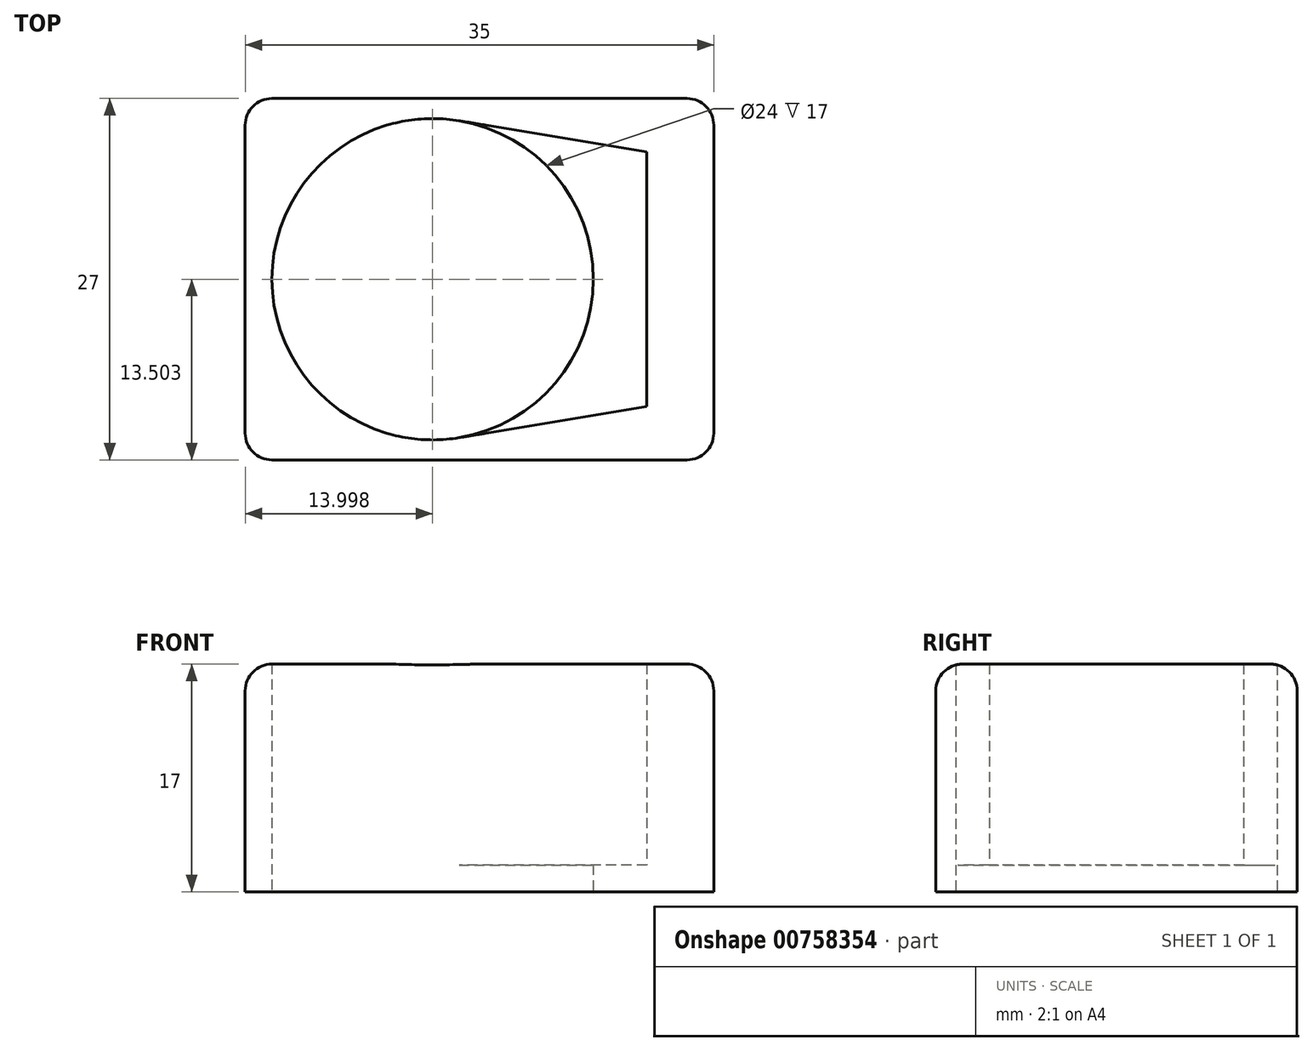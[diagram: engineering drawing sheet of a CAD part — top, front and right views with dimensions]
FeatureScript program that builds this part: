
annotation { "Feature Type Name" : "Feature", "Feature Type Description" : "" }
export const myFeature = defineFeature(function(context is Context, id is Id, definition is map)
    precondition{}
    {
        {
            var Q0;
            Q0=qCreatedBy(makeId("Top.planeOp"),FACE);
            var sketch = newSketch(context, id + "F0", { "sketchPlane" : qUnion([Q0])});
            skLineSegment(sketch, "E0", {"start": v(-0.7, 17.13) * mm, "end": v(-0.7, -1.87) * mm});
            skLineSegment(sketch, "E1", {"start": v(-0.7, 7.63) * mm, "end": v(-28.7, 7.63) * mm});
            skCircle(sketch, "E2", {"center": v(-16.7, 7.63) * mm, "radius": 12 * mm});
            skPoint(sketch, "E2.first.point", {"position": v(-8.44, 16.33) * mm});
            skPoint(sketch, "E2.third.point", {"position": v(-13.92, -4.04) * mm});
            skLineSegment(sketch, "E3", {"start": v(-0.7, 17.13) * mm, "end": v(-14.73, 19.47) * mm});
            skLineSegment(sketch, "E4", {"start": v(-0.7, -1.87) * mm, "end": v(-14.73, -4.2) * mm});
            skLineSegment(sketch, "E5.bottom", {"start": v(-30.7, 21.13) * mm, "end": v(4.3, 21.13) * mm});
            skLineSegment(sketch, "E5.top", {"start": v(-30.7, -5.87) * mm, "end": v(4.3, -5.87) * mm});
            skLineSegment(sketch, "E5.left", {"start": v(-30.7, 21.13) * mm, "end": v(-30.7, -5.87) * mm});
            skLineSegment(sketch, "E5.right", {"start": v(4.3, 21.13) * mm, "end": v(4.3, -5.87) * mm});
            skPoint(sketch, "E6", {"position": v(-28.7, 7.63) * mm});
            skPoint(sketch, "E7", {"position": v(-30.7, 7.63) * mm});
            skSolve(sketch);
        }
        {
            var Q0;
            {var subQ6=sQuery(id+"F0.wireOp",EDGE,"E3");Q0=makeQuery(id+"F0.imprint","IMPRINT",FACE,{"disambiguationData":[TD([[makeQuery(id+"F0.imprint","IMPRINT",EDGE,{"derivedFrom":subQ6}),-1.0]])]});}
            extrude(context, id + "F1", {"entities" : qUnion([Q0]), "depth" : 15 * mm, "offsetDistance" : 25 * mm});
        }
        {
            var Q0;
            {var subQ6=sQuery(id+"F0.wireOp",EDGE,"E3");Q0=makeQuery(id+"F0.imprint","IMPRINT",FACE,{"disambiguationData":[TD([[makeQuery(id+"F0.imprint","IMPRINT",EDGE,{"derivedFrom":subQ6}),-1.0]])]});}
            var Q1;
            {var subQ0=sQuery(id+"F0.wireOp",EDGE,"E2");var subQ1=sQuery(id+"F0.wireOp",EDGE,"E1");var subQ2=makeQuery(id+"F0.imprint","INTERSECT",VERTEX,{"disambiguationData":[OD(0.0)],"derivedFrom":[subQ1,subQ0]});Q1=makeQuery(id+"F0.imprint","IMPRINT",FACE,{"disambiguationData":[TD([[makeQuery(id+"F0.imprint","IMPRINT",EDGE,{"disambiguationData":[TD([[subQ2,1.0]])],"derivedFrom":subQ1}),1.0]])]});}
            var Q2;
            {var subQ0=sQuery(id+"F0.wireOp",EDGE,"E2");var subQ1=sQuery(id+"F0.wireOp",EDGE,"E1");var subQ2=makeQuery(id+"F0.imprint","INTERSECT",VERTEX,{"disambiguationData":[OD(0.0)],"derivedFrom":[subQ1,subQ0]});Q2=makeQuery(id+"F0.imprint","IMPRINT",FACE,{"disambiguationData":[TD([[makeQuery(id+"F0.imprint","IMPRINT",EDGE,{"disambiguationData":[TD([[subQ2,1.0]])],"derivedFrom":subQ1}),-1.0]])]});}
            var Q3;
            {var subQ0=sQuery(id+"F0.wireOp",EDGE,"E3");Q3=makeQuery(id+"F0.imprint","IMPRINT",FACE,{"disambiguationData":[TD([[makeQuery(id+"F0.imprint","IMPRINT",EDGE,{"derivedFrom":subQ0}),1.0]])]});}
            var Q4;
            {var subQ0=sQuery(id+"F0.wireOp",EDGE,"E4");Q4=makeQuery(id+"F0.imprint","IMPRINT",FACE,{"disambiguationData":[TD([[makeQuery(id+"F0.imprint","IMPRINT",EDGE,{"derivedFrom":subQ0}),-1.0]])]});}
            extrude(context, id + "F2", {"entities" : qUnion([Q0, Q1, Q2, Q3, Q4]), "operationType" : NewBodyOperationType.ADD, "depth" : -2 * mm, "offsetDistance" : 25 * mm});
        }
        {
            var Q0;
            {var subQ0=sQuery(id+"F0.wireOp",EDGE,"E5.left");var subQ1=sQuery(id+"F0.wireOp",EDGE,"E5.top");Q0=makeQuery(id+"F2.boolean.opBoolean","MERGE",EDGE,{"derivedFrom":[makeQuery(id+"F1.opExtrude","SWEPT_EDGE",EDGE,{"disambiguationData":[OSD([subQ1,subQ0])]}),makeQuery(id+"F2.opExtrude","SWEPT_EDGE",EDGE,{"disambiguationData":[OSD([subQ1,subQ0])]})]});}
            var Q1;
            Q1=makeQuery(id+"F1.opExtrude","CAP_EDGE",EDGE,{"disambiguationData":[OSD([sQuery(id+"F0.wireOp",EDGE,"E5.top")])],"isStart":false});
            var Q2;
            {var subQ0=sQuery(id+"F0.wireOp",EDGE,"E5.right");var subQ1=sQuery(id+"F0.wireOp",EDGE,"E5.top");Q2=makeQuery(id+"F2.boolean.opBoolean","MERGE",EDGE,{"derivedFrom":[makeQuery(id+"F1.opExtrude","SWEPT_EDGE",EDGE,{"disambiguationData":[OSD([subQ1,subQ0])]}),makeQuery(id+"F2.opExtrude","SWEPT_EDGE",EDGE,{"disambiguationData":[OSD([subQ1,subQ0])]})]});}
            var Q3;
            Q3=makeQuery(id+"F1.opExtrude","CAP_EDGE",EDGE,{"disambiguationData":[OSD([sQuery(id+"F0.wireOp",EDGE,"E5.right")])],"isStart":false});
            var Q4;
            {var subQ0=sQuery(id+"F0.wireOp",EDGE,"E5.right");var subQ1=sQuery(id+"F0.wireOp",EDGE,"E5.bottom");Q4=makeQuery(id+"F2.boolean.opBoolean","MERGE",EDGE,{"derivedFrom":[makeQuery(id+"F1.opExtrude","SWEPT_EDGE",EDGE,{"disambiguationData":[OSD([subQ1,subQ0])]}),makeQuery(id+"F2.opExtrude","SWEPT_EDGE",EDGE,{"disambiguationData":[OSD([subQ1,subQ0])]})]});}
            var Q5;
            {var subQ0=sQuery(id+"F0.wireOp",EDGE,"E5.left");var subQ1=sQuery(id+"F0.wireOp",EDGE,"E5.bottom");Q5=makeQuery(id+"F2.boolean.opBoolean","MERGE",EDGE,{"derivedFrom":[makeQuery(id+"F1.opExtrude","SWEPT_EDGE",EDGE,{"disambiguationData":[OSD([subQ1,subQ0])]}),makeQuery(id+"F2.opExtrude","SWEPT_EDGE",EDGE,{"disambiguationData":[OSD([subQ1,subQ0])]})]});}
            var Q6;
            Q6=makeQuery(id+"F1.opExtrude","CAP_EDGE",EDGE,{"disambiguationData":[OSD([sQuery(id+"F0.wireOp",EDGE,"E5.bottom")])],"isStart":false});
            var Q7;
            Q7=makeQuery(id+"F1.opExtrude","CAP_EDGE",EDGE,{"disambiguationData":[OSD([sQuery(id+"F0.wireOp",EDGE,"E5.left")])],"isStart":false});
            fillet(context, id + "F3", {"entities" : qUnion([Q0, Q1, Q2, Q3, Q4, Q5, Q6, Q7]), "radius" : 2 * mm, "tangentPropagation" : true, "allowEdgeOverflow" : false});
        }
    });
